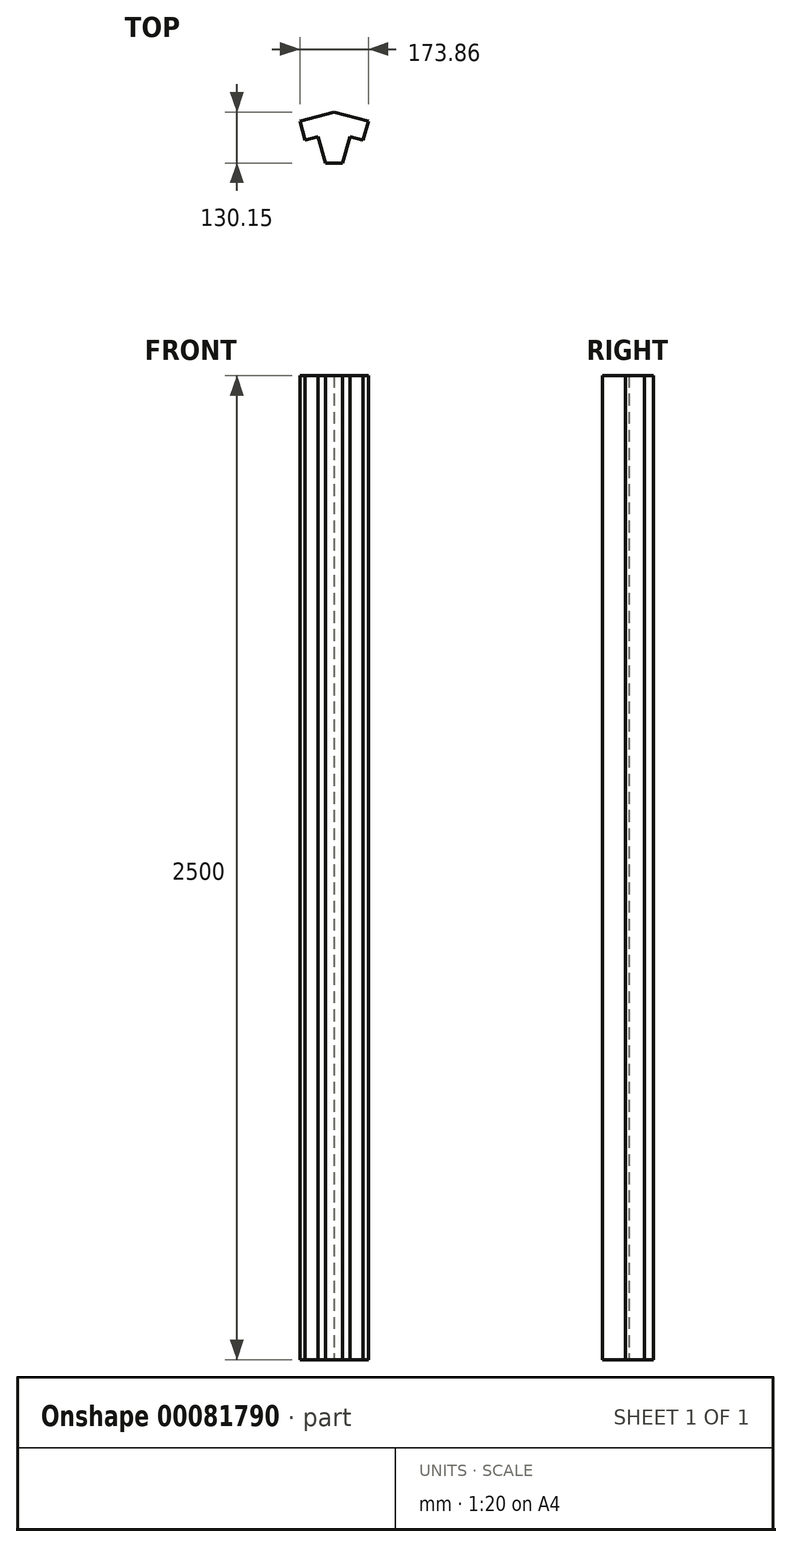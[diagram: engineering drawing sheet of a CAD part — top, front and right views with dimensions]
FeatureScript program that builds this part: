
annotation { "Feature Type Name" : "Feature", "Feature Type Description" : "" }
export const myFeature = defineFeature(function(context is Context, id is Id, definition is map)
    precondition{}
    {
        {
            var Q0;
            Q0=qCreatedBy(makeId("Top.planeOp"),FACE);
            var sketch = newSketch(context, id + "F0", { "sketchPlane" : qUnion([Q0])});
            skLineSegment(sketch, "E0", {"start": v(-22.07, 0) * mm, "end": v(22.07, 0) * mm});
            skLineSegment(sketch, "E1", {"start": v(22.07, 0) * mm, "end": v(40.18, 67.61) * mm});
            skLineSegment(sketch, "E2", {"start": v(40.18, 67.61) * mm, "end": v(74, 58.56) * mm});
            skLineSegment(sketch, "E3", {"start": v(74, 58.56) * mm, "end": v(86.93, 106.85) * mm});
            skLineSegment(sketch, "E4", {"start": v(86.93, 106.85) * mm, "end": v(0, 130.15) * mm});
            skLineSegment(sketch, "E5", {"start": v(0, 130.15) * mm, "end": v(-86.93, 106.85) * mm});
            skLineSegment(sketch, "E6", {"start": v(-86.93, 106.85) * mm, "end": v(-74, 58.56) * mm});
            skLineSegment(sketch, "E7", {"start": v(-40.18, 67.61) * mm, "end": v(-22.07, 0) * mm});
            skLineSegment(sketch, "E8", {"start": v(0, 130.15) * mm, "end": v(0, 0) * mm, "construction": true});
            skPoint(sketch, "E9", {"position": v(0, 0) * mm});
            skLineSegment(sketch, "E10", {"start": v(-74, 58.56) * mm, "end": v(-40.18, 67.61) * mm});
            skSolve(sketch);
        }
        {
            var Q0;
            Q0=makeQuery(id+"F0.imprint","IMPRINT",FACE,{"disambiguationData":[TD([[makeQuery(id+"F0.imprint","IMPRINT",EDGE,{"derivedFrom":sQuery(id+"F0.wireOp",EDGE,"E0")}),1.0]])]});
            extrude(context, id + "F1", {"entities" : qUnion([Q0]), "depth" : 2500 * mm});
        }
    });
